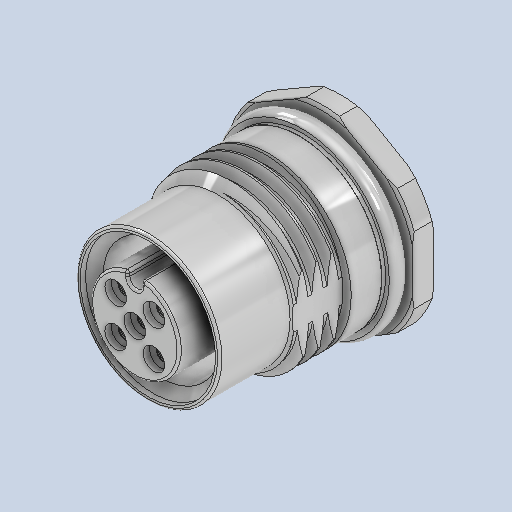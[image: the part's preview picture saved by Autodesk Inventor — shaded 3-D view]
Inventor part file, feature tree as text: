
AUTODESK INVENTOR PART (.ipt)
format: ipt  version: 2024.2 (Build 282272000, 272)  size: 755,712 bytes
history: native  units: mm
features: extrude x1, sketch x1, imported_body x1
ambient origin geometry x8: Origin, YZ Plane, XZ Plane, XY Plane, X Axis, Y Axis, Z Axis, Center Point
bodies: Solid1 (feature_tree)
feature tree (3):
  extrude  "Extrusion1"  [1 undecoded]
  sketch  "Sketch2"  dims[d0=0.0mm d1=0.0mm]
  imported_body  "Base1"
note: 1 required parameter value undecoded (feature->parameter linkage not recoverable at this tier; creation-order binding heuristic only, values carry confidence <= 0.55)
